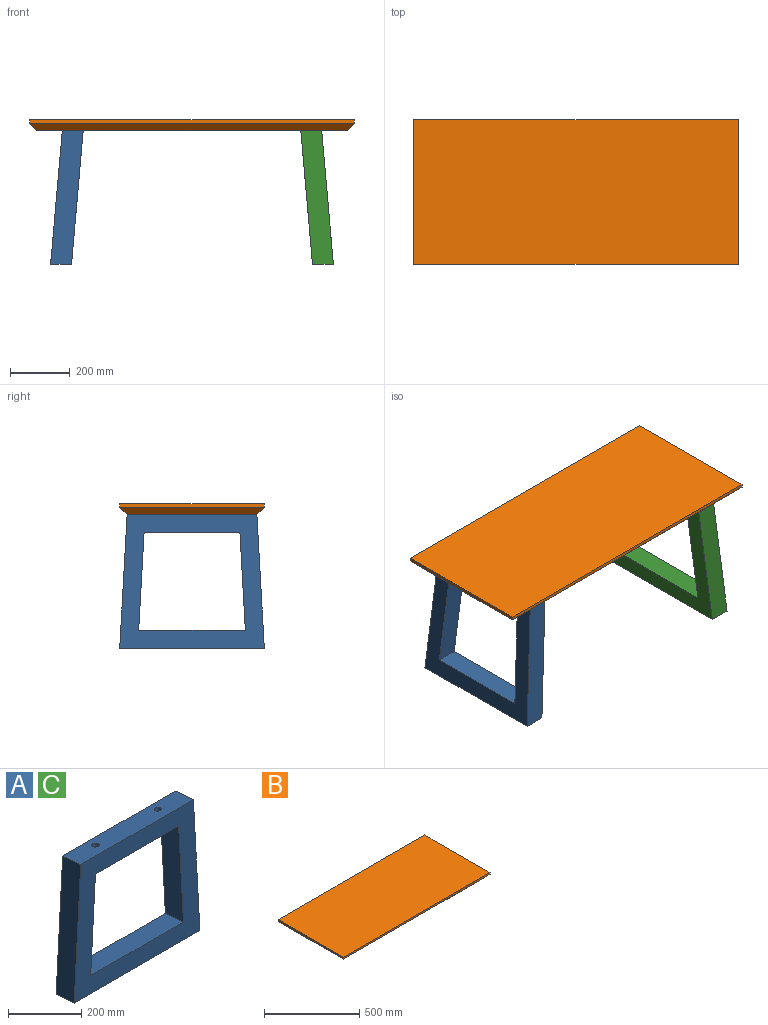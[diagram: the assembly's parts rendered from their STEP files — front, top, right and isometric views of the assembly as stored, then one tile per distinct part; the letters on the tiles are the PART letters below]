
ASSEMBLY  parts=3 mates=2
PART A: 16 faces, bbox 485x69.7x456.1 mm
  f0: cylinder r=10mm len=41.36mm, axis (0,-0.09,-1), area 2498.9mm2, adj f11,f15
  f1: cylinder r=10mm len=41.36mm, axis (0,-0.09,-1), area 2498.9mm2, adj f11,f13
  f2: plane 336.1x69.73mm, normal (1,0,-0.06), area 23047.9mm2, adj f3,f5,f6,f7
  f3: plane 321.48x69.73mm, normal (0,-0.09,-1), area 19990.4mm2, adj f2,f4,f6,f7,f12,f14
  f4: plane 336.1x69.73mm, normal (-1,0,-0.06), area 23047.9mm2, adj f3,f5,f6,f7
  f5: plane 358.15x69.73mm, normal (0,0.09,1), area 25070.4mm2, adj f2,f4,f6,f7
  f6: plane 485x450mm, normal (0,1,0), area 94861.1mm2, adj f2,f3,f4,f5,f8,f9,f10,f11
  f7: plane 485x450mm, normal (0,-1,0), area 94861.1mm2, adj f2,f3,f4,f5,f8,f9,f10,f11
  f8: plane 456.1x69.73mm, normal (-1,0,0.06), area 31428.9mm2, adj f6,f7,f9,f11
  f9: plane 485x69.73mm, normal (0,-0.09,-1), area 33950mm2, adj f6,f7,f8,f10
  f10: plane 456.1x69.73mm, normal (1,0,0.06), area 31428.9mm2, adj f6,f7,f9,f11
  f11: plane 435x69.73mm, normal (0,0.09,1), area 29821.7mm2, adj f0,f1,f6,f7,f8,f10
  f12: cylinder r=20mm len=41.59mm, axis (0,-0.09,-1), area 2513.3mm2, adj f3,f13
  f13: plane 40x39.85mm, normal (0,-0.09,-1), area 942.5mm2, adj f1,f12
  f14: cylinder r=20mm len=41.59mm, axis (0,-0.09,-1), area 2513.3mm2, adj f3,f15
  f15: plane 40x39.85mm, normal (0,-0.09,-1), area 942.5mm2, adj f0,f14
PART B: 10 faces, bbox 1090x485x36 mm
  f0: plane 485x11mm, normal (1,0,0), area 5335mm2, adj f1,f3,f4,f6
  f1: plane 1090x11mm, normal (0,1,0), area 11990mm2, adj f0,f2,f4,f7
  f2: plane 485x11mm, normal (-1,0,0), area 5335mm2, adj f1,f3,f4,f9
  f3: plane 1090x11mm, normal (0,-1,0), area 11990mm2, adj f0,f2,f4,f8
  f4: plane 1090x485mm, normal (0,0,1), area 528650mm2, adj f0,f1,f2,f3
  f5: plane 1040x435mm, normal (0,0,-1), area 452400mm2, adj f6,f7,f8,f9
  f6: plane 485x25mm, normal (0.71,0,-0.71), area 16263.5mm2, adj f0,f5,f7,f8
  f7: plane 1090x25mm, normal (0,0.71,-0.71), area 37653.4mm2, adj f1,f5,f6,f9
  f8: plane 1090x25mm, normal (0,-0.71,-0.71), area 37653.4mm2, adj f3,f5,f6,f9
  f9: plane 485x25mm, normal (-0.71,0,-0.71), area 16263.5mm2, adj f2,f5,f7,f8
PART C: same geometry as A
PLACE A rot(axis=(0.04,0.04,1),90.1deg) t=(-685.57,-301.09,-363.97)mm
PLACE B t=(-211.35,-58.59,84.32)mm
PLACE C rot(axis=(0.04,-0.04,-1),90.1deg) t=(262.87,183.91,-363.97)mm
MATE fastened C.f11 <-> B.f5  axis (0,0,1) through (188.65,-58.59,84.32)mm
MATE fastened A.f11 <-> B.f5  axis (0,0,1) through (-611.35,-58.59,84.32)mm
